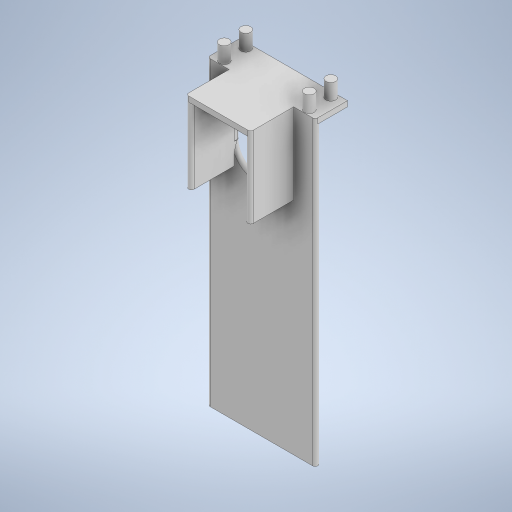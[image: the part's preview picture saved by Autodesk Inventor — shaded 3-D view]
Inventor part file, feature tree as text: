
AUTODESK INVENTOR PART (.ipt)
format: ipt  version: 2023 (Build 270158000, 158)  size: 357,888 bytes
history: native  units: mm
features: extrude x7, sketch x7, fillet x2
ambient origin geometry x8: Origin, YZ Plane, XZ Plane, XY Plane, X Axis, Y Axis, Z Axis, Center Point
bodies: Solid1 (feature_tree)
feature tree (16):
  extrude  "Extrusion1"  Depth=200.0mm
  extrude  "Extrusion6"  Depth=50.0mm
  sketch  "Sketch15"  dims[d22=50.0mm d23=20.0mm]
  sketch  "Sketch16"  dims[d24=5.0mm d25=0.0mm d46=100.0mm]
  extrude  "Extrusion11"  Depth=20.0mm
  extrude  "Extrusion12"  Depth=100.0mm
  extrude  "Extrusion17"  Depth=9.0mm
  extrude  "Extrusion18"  Depth=9.0mm
  extrude  "Extrusion19"  Depth=2.5mm TaperAngle=0.0deg
  fillet  "Fillet1"  Radius=15.0mm
  fillet  "Fillet2"  Radius=100.0mm
  sketch  "Sketch1"  dims[d0=100.0mm d1=200.0mm]
  sketch  "Sketch6"  dims[d2=5.0mm d3=0.0mm d21=50.0mm]
  sketch  "Sketch21"  dims[d47=30.0mm d48=9.0mm]
  sketch  "Sketch23"  dims[d49=9.0mm d50=9.0mm]
  sketch  "Sketch24"  dims[d51=9.0mm d52=5.0mm d53=0.0mm d54=15.0mm d55=0.0mm d66=100.0mm d67=80.0mm d68=5.0mm d69=0.0mm d72=60.0mm d73=75.0mm d74=40.0mm d75=0.0mm d76=50.0mm d77=40.0mm d78=0.0mm d79=2.5mm d80=2.5mm d81=0.0mm d82=0.0mm]
